# Revit family: Alcorque Ecológico
name_source: partatom
category: Furniture
units: mm (PartAtom-declared; Revit-internal decimal feet)

## family parameters
Always vertical = Yes
Cut with Voids When Loaded = No
Room Calculation Point = No
Shared = No
Work Plane-Based = No

## types (3) — shared parameters
Description = Alcorque Ecológico fabricado en ReBnew plástico reciclado de alta calidad, 100% Reciclable, Recuperable y Reutilizable.
Fabricante = BENITO URBAN SL
Ficha técnica = https://www.benito.com
H = 0.06 m
Material = ReBnew plástico
Type Comments = SIN MANTENIMIENTO. Resistente a la intermperie, al agua del mar (no se pudre), a los rayos UV., no se astilla, no hay que pintarlo. Libre de
sustancias contaminantes.
URL Producto = https://www.benito.com
zero-valued in all types: Default Elevation

## per-type parameters (varying)
| type | A | A50 | A51 | A52 | B | Referencia |
| Alcorque Ecológico-A50-1000mm | 1 m | Yes | No | No | 1 m | A50 |
| Alcorque Ecológico-A51-1500mm | 1.5 m | No | Yes | No | 1.5 m | A51 |
| Alcorque Ecológico-A52-2000mm | 2 m | No | No | Yes | 2 m | A52 |

## geometry (parser evidence)
native form markers: Blend x2, Sweep x1
no freeform markers — native parametric forms only
